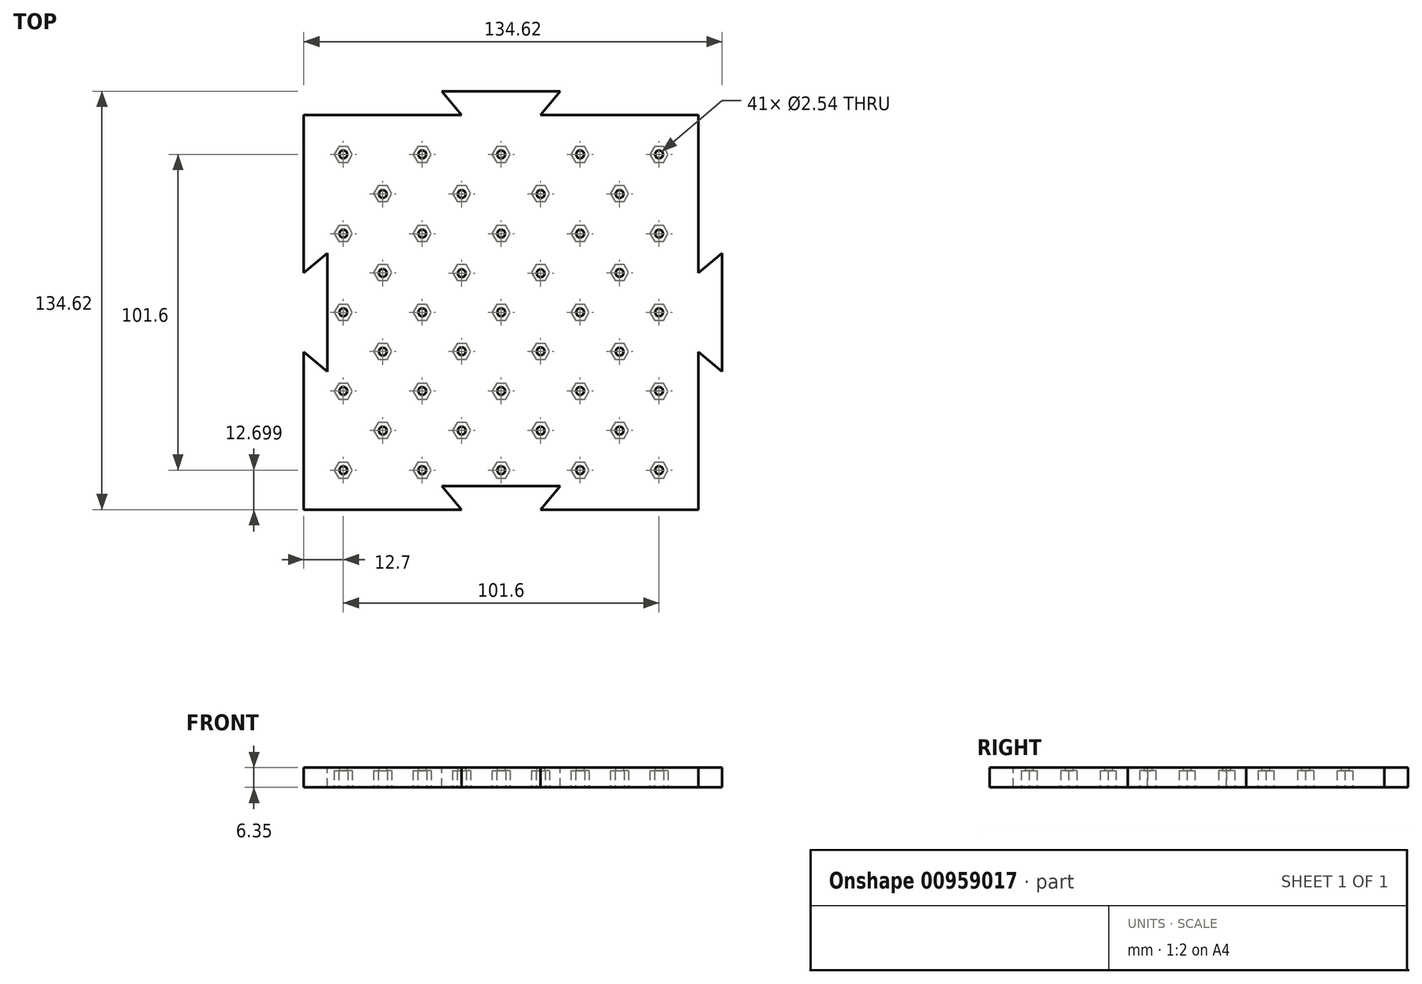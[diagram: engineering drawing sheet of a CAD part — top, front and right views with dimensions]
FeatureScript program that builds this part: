
annotation { "Feature Type Name" : "Feature", "Feature Type Description" : "" }
export const myFeature = defineFeature(function(context is Context, id is Id, definition is map)
    precondition{}
    {
        {
            var Q0;
            Q0=qCreatedBy(makeId("Top.planeOp"),FACE);
            var sketch = newSketch(context, id + "F0", { "sketchPlane" : qUnion([Q0])});
            skLineSegment(sketch, "E0.bottom", {"start": v(63.5, 63.69) * mm, "end": v(-63.5, 63.69) * mm});
            skLineSegment(sketch, "E0.top", {"start": v(63.5, -63.31) * mm, "end": v(-63.5, -63.31) * mm});
            skLineSegment(sketch, "E0.left", {"start": v(63.5, 63.69) * mm, "end": v(63.5, -63.31) * mm});
            skLineSegment(sketch, "E0.right", {"start": v(-63.5, 63.69) * mm, "end": v(-63.5, -63.31) * mm});
            skLineSegment(sketch, "E1", {"start": v(-50.8, 50.99) * mm, "end": v(50.8, 50.99) * mm, "construction": true});
            skLineSegment(sketch, "E2", {"start": v(-50.8, 50.99) * mm, "end": v(-50.8, -50.61) * mm, "construction": true});
            skLineSegment(sketch, "E3", {"start": v(-50.8, -50.61) * mm, "end": v(50.8, -50.61) * mm, "construction": true});
            skLineSegment(sketch, "E4", {"start": v(50.8, 50.99) * mm, "end": v(50.8, -50.61) * mm, "construction": true});
            skLineSegment(sketch, "E5", {"start": v(0, 50.99) * mm, "end": v(0, -50.61) * mm, "construction": true});
            skLineSegment(sketch, "E6", {"start": v(25.4, 50.99) * mm, "end": v(25.4, -50.61) * mm, "construction": true});
            skLineSegment(sketch, "E7", {"start": v(-50.8, 0.19) * mm, "end": v(50.8, 0.19) * mm, "construction": true});
            skLineSegment(sketch, "E8", {"start": v(-50.8, 0.19) * mm, "end": v(-25.4, 25.5) * mm, "construction": true});
            skLineSegment(sketch, "E9", {"start": v(-25.4, 25.5) * mm, "end": v(0, 50.99) * mm, "construction": true});
            skLineSegment(sketch, "E10", {"start": v(0, 0) * mm, "end": v(-25.4, 25.5) * mm, "construction": true});
            skLineSegment(sketch, "E11", {"start": v(-50.8, 50.99) * mm, "end": v(-25.4, 25.5) * mm, "construction": true});
            skLineSegment(sketch, "E12", {"start": v(-25.4, 50.99) * mm, "end": v(-25.4, -50.61) * mm, "construction": true});
            skCircle(sketch, "E13", {"center": v(-38.1, 38.24) * mm, "radius": 1.27 * mm});
            skCircle(sketch, "E14", {"center": v(-12.7, 38.24) * mm, "radius": 1.27 * mm});
            skCircle(sketch, "E15", {"center": v(-25.4, 25.5) * mm, "radius": 1.27 * mm});
            skCircle(sketch, "E16", {"center": v(-12.7, 12.75) * mm, "radius": 1.27 * mm});
            skCircle(sketch, "E17", {"center": v(-38.1, 12.84) * mm, "radius": 1.27 * mm});
            skCircle(sketch, "E18", {"center": v(0, 25.5) * mm, "radius": 1.27 * mm});
            skCircle(sketch, "E19", {"center": v(-25.4, 0.19) * mm, "radius": 1.27 * mm});
            skCircle(sketch, "E20.MirrorC", {"center": v(12.7, 38.24) * mm, "radius": 1.27 * mm});
            skCircle(sketch, "E21.MirrorC", {"center": v(25.4, 25.5) * mm, "radius": 1.27 * mm});
            skCircle(sketch, "E22.MirrorC", {"center": v(38.1, 38.24) * mm, "radius": 1.27 * mm});
            skLineSegment(sketch, "E23.MirrorCS", {"start": v(25.4, 25.5) * mm, "end": v(0, 50.99) * mm, "construction": true});
            skLineSegment(sketch, "E24.MirrorCS", {"start": v(50.8, 50.99) * mm, "end": v(25.4, 25.5) * mm, "construction": true});
            skLineSegment(sketch, "E25.MirrorCS", {"start": v(0, 0) * mm, "end": v(25.4, 25.5) * mm, "construction": true});
            skLineSegment(sketch, "E26.MirrorCS", {"start": v(50.8, 0.19) * mm, "end": v(25.4, 25.5) * mm, "construction": true});
            skCircle(sketch, "E27.MirrorC", {"center": v(38.1, 12.84) * mm, "radius": 1.27 * mm});
            skCircle(sketch, "E28.MirrorC", {"center": v(12.7, 12.75) * mm, "radius": 1.27 * mm});
            skCircle(sketch, "E29.MirrorC", {"center": v(-25.4, -25.12) * mm, "radius": 1.27 * mm});
            skCircle(sketch, "E30.MirrorC", {"center": v(25.4, -25.12) * mm, "radius": 1.27 * mm});
            skCircle(sketch, "E31.MirrorC", {"center": v(12.7, -37.86) * mm, "radius": 1.27 * mm});
            skCircle(sketch, "E32.MirrorC", {"center": v(-38.1, -12.46) * mm, "radius": 1.27 * mm});
            skLineSegment(sketch, "E33.MirrorCS", {"start": v(25.4, -50.61) * mm, "end": v(25.4, 50.99) * mm, "construction": true});
            skCircle(sketch, "E34.MirrorC", {"center": v(-38.1, -37.86) * mm, "radius": 1.27 * mm});
            skCircle(sketch, "E35.MirrorC", {"center": v(38.1, -12.46) * mm, "radius": 1.27 * mm});
            skCircle(sketch, "E36.MirrorC", {"center": v(0, -25.12) * mm, "radius": 1.27 * mm});
            skCircle(sketch, "E37.MirrorC", {"center": v(-12.7, -37.86) * mm, "radius": 1.27 * mm});
            skCircle(sketch, "E38.MirrorC", {"center": v(38.1, -37.86) * mm, "radius": 1.27 * mm});
            skCircle(sketch, "E39.MirrorC", {"center": v(-12.7, -12.37) * mm, "radius": 1.27 * mm});
            skCircle(sketch, "E40.MirrorC", {"center": v(12.7, -12.37) * mm, "radius": 1.27 * mm});
            skLineSegment(sketch, "E41.MirrorCS", {"start": v(-25.4, -25.12) * mm, "end": v(0, -50.61) * mm, "construction": true});
            skLineSegment(sketch, "E42.MirrorCS", {"start": v(50.8, -50.61) * mm, "end": v(25.4, -25.12) * mm, "construction": true});
            skLineSegment(sketch, "E43.MirrorCS", {"start": v(-50.8, -50.61) * mm, "end": v(-25.4, -25.12) * mm, "construction": true});
            skLineSegment(sketch, "E44.MirrorCS", {"start": v(50.8, 0.19) * mm, "end": v(25.4, -25.12) * mm, "construction": true});
            skLineSegment(sketch, "E45.MirrorCS", {"start": v(0, 0.38) * mm, "end": v(25.4, -25.12) * mm, "construction": true});
            skLineSegment(sketch, "E46.MirrorCS", {"start": v(0, -50.61) * mm, "end": v(0, 50.99) * mm, "construction": true});
            skLineSegment(sketch, "E47.MirrorCS", {"start": v(-25.4, -50.61) * mm, "end": v(-25.4, 50.99) * mm, "construction": true});
            skLineSegment(sketch, "E48.MirrorCS", {"start": v(0, 0.38) * mm, "end": v(-25.4, -25.12) * mm, "construction": true});
            skLineSegment(sketch, "E49.MirrorCS", {"start": v(25.4, -25.12) * mm, "end": v(0, -50.61) * mm, "construction": true});
            skLineSegment(sketch, "E50.MirrorCS", {"start": v(-50.8, 0.19) * mm, "end": v(-25.4, -25.12) * mm, "construction": true});
            skCircle(sketch, "E51.MirrorC", {"center": v(25.4, 0.19) * mm, "radius": 1.27 * mm});
            skCircle(sketch, "E52", {"center": v(-50.8, 0.19) * mm, "radius": 1.27 * mm});
            skCircle(sketch, "E53", {"center": v(-50.8, -25.12) * mm, "radius": 1.27 * mm});
            skCircle(sketch, "E54", {"center": v(-50.8, 25.5) * mm, "radius": 1.27 * mm});
            skCircle(sketch, "E55", {"center": v(-50.8, 50.99) * mm, "radius": 1.27 * mm});
            skCircle(sketch, "E56", {"center": v(-50.8, -50.61) * mm, "radius": 1.27 * mm});
            skCircle(sketch, "E57", {"center": v(-25.4, -50.61) * mm, "radius": 1.27 * mm});
            skCircle(sketch, "E58", {"center": v(0, -50.61) * mm, "radius": 1.27 * mm});
            skCircle(sketch, "E59", {"center": v(25.4, -50.61) * mm, "radius": 1.27 * mm});
            skCircle(sketch, "E60", {"center": v(50.8, -50.61) * mm, "radius": 1.27 * mm});
            skCircle(sketch, "E61", {"center": v(50.8, -25.12) * mm, "radius": 1.27 * mm});
            skCircle(sketch, "E62", {"center": v(50.8, 0.19) * mm, "radius": 1.27 * mm});
            skCircle(sketch, "E63", {"center": v(50.8, 25.5) * mm, "radius": 1.27 * mm});
            skCircle(sketch, "E64", {"center": v(50.8, 50.99) * mm, "radius": 1.27 * mm});
            skCircle(sketch, "E65", {"center": v(25.4, 50.99) * mm, "radius": 1.27 * mm});
            skCircle(sketch, "E66", {"center": v(0, 50.99) * mm, "radius": 1.27 * mm});
            skCircle(sketch, "E67", {"center": v(-25.4, 50.99) * mm, "radius": 1.27 * mm});
            skCircle(sketch, "E68", {"center": v(0, 0.19) * mm, "radius": 1.27 * mm});
            skSolve(sketch);
        }
        {
            var Q0;
            Q0=makeQuery(id+"F0.imprint","IMPRINT",FACE,{"disambiguationData":[TD([[makeQuery(id+"F0.imprint","IMPRINT",EDGE,{"derivedFrom":sQuery(id+"F0.wireOp",EDGE,"E0.bottom")}),1.0]])]});
            extrude(context, id + "F1", {"entities" : qUnion([Q0]), "depth" : 6.35 * mm, "offsetDistance" : 25.4 * mm});
        }
        {
            var Q0;
            Q0=makeQuery(id+"F1.opExtrude","CAP_FACE",FACE,{"disambiguationData":[OSD([sQuery(id+"F0.wireOp",EDGE,"E0.bottom"),sQuery(id+"F0.wireOp",EDGE,"E0.top"),sQuery(id+"F0.wireOp",EDGE,"E0.left"),sQuery(id+"F0.wireOp",EDGE,"E0.right"),sQuery(id+"F0.wireOp",EDGE,"Hy7Gs1fu-bPC3-lwsH-q5tp-A8iLxPEHDNgU"),sQuery(id+"F0.wireOp",EDGE,"OdMErub8-gENd-RMHu-1Eyq-STtZkmv1sPD6"),sQuery(id+"F0.wireOp",EDGE,"gUio85Hi-duiy-LhhE-UZof-TjOPB2Q9psdY"),sQuery(id+"F0.wireOp",EDGE,"tl9tluQc-fSzx-BFO9-yEud-i3mXb7KbXmNx"),sQuery(id+"F0.wireOp",EDGE,"GmsfjQEB-c2r3-9ydc-1yJa-UPbpGBDKNwxx"),sQuery(id+"F0.wireOp",EDGE,"eb66b9ba-c206-47c9-b1f8-58a300546e6e.0.1.0"),sQuery(id+"F0.wireOp",EDGE,"eb66b9ba-c206-47c9-b1f8-58a300546e6e.0.1.1"),sQuery(id+"F0.wireOp",EDGE,"eb66b9ba-c206-47c9-b1f8-58a300546e6e.0.1.2"),sQuery(id+"F0.wireOp",EDGE,"eb66b9ba-c206-47c9-b1f8-58a300546e6e.0.1.3"),sQuery(id+"F0.wireOp",EDGE,"eb66b9ba-c206-47c9-b1f8-58a300546e6e.0.1.4"),sQuery(id+"F0.wireOp",EDGE,"eb66b9ba-c206-47c9-b1f8-58a300546e6e.1.0.0"),sQuery(id+"F0.wireOp",EDGE,"eb66b9ba-c206-47c9-b1f8-58a300546e6e.1.0.1"),sQuery(id+"F0.wireOp",EDGE,"eb66b9ba-c206-47c9-b1f8-58a300546e6e.1.0.2"),sQuery(id+"F0.wireOp",EDGE,"eb66b9ba-c206-47c9-b1f8-58a300546e6e.1.0.3"),sQuery(id+"F0.wireOp",EDGE,"eb66b9ba-c206-47c9-b1f8-58a300546e6e.1.0.4"),sQuery(id+"F0.wireOp",EDGE,"eb66b9ba-c206-47c9-b1f8-58a300546e6e.1.1.0"),sQuery(id+"F0.wireOp",EDGE,"eb66b9ba-c206-47c9-b1f8-58a300546e6e.1.1.1"),sQuery(id+"F0.wireOp",EDGE,"eb66b9ba-c206-47c9-b1f8-58a300546e6e.1.1.2"),sQuery(id+"F0.wireOp",EDGE,"eb66b9ba-c206-47c9-b1f8-58a300546e6e.1.1.3"),sQuery(id+"F0.wireOp",EDGE,"eb66b9ba-c206-47c9-b1f8-58a300546e6e.1.1.4")])],"isStart":true});
            var sketch = newSketch(context, id + "F2", { "sketchPlane" : qUnion([Q0])});
            skCircle(sketch, "E69.cCircle", {"center": v(-50.8, 50.61) * mm, "radius": 2.54 * mm, "construction": true});
            skLineSegment(sketch, "E69.0", {"start": v(-52.27, 53.15) * mm, "end": v(-49.33, 53.15) * mm});
            skLineSegment(sketch, "E69.1", {"start": v(-49.33, 53.15) * mm, "end": v(-47.87, 50.61) * mm});
            skLineSegment(sketch, "E69.2", {"start": v(-47.87, 50.61) * mm, "end": v(-49.33, 48.07) * mm});
            skLineSegment(sketch, "E69.3", {"start": v(-49.33, 48.07) * mm, "end": v(-52.27, 48.07) * mm});
            skLineSegment(sketch, "E69.4", {"start": v(-52.27, 48.07) * mm, "end": v(-53.73, 50.61) * mm});
            skLineSegment(sketch, "E69.5", {"start": v(-53.73, 50.61) * mm, "end": v(-52.27, 53.15) * mm});
            skPoint(sketch, "E69.0.midPoint", {"position": v(-50.8, 53.15) * mm});
            skCircle(sketch, "E70.cCircle", {"center": v(-38.1, 37.86) * mm, "radius": 2.54 * mm, "construction": true});
            skLineSegment(sketch, "E70.0", {"start": v(-39.57, 40.4) * mm, "end": v(-36.63, 40.4) * mm});
            skLineSegment(sketch, "E70.1", {"start": v(-36.63, 40.4) * mm, "end": v(-35.17, 37.86) * mm});
            skLineSegment(sketch, "E70.2", {"start": v(-35.17, 37.86) * mm, "end": v(-36.63, 35.32) * mm});
            skLineSegment(sketch, "E70.3", {"start": v(-36.63, 35.32) * mm, "end": v(-39.57, 35.32) * mm});
            skLineSegment(sketch, "E70.4", {"start": v(-39.57, 35.32) * mm, "end": v(-41.03, 37.86) * mm});
            skLineSegment(sketch, "E70.5", {"start": v(-41.03, 37.86) * mm, "end": v(-39.57, 40.4) * mm});
            skPoint(sketch, "E70.0.midPoint", {"position": v(-38.1, 40.4) * mm});
            skCircle(sketch, "E71.0.1.0", {"center": v(-38.1, 12.46) * mm, "radius": 2.54 * mm, "construction": true});
            skLineSegment(sketch, "E71.0.1.1", {"start": v(-36.63, 15) * mm, "end": v(-35.17, 12.46) * mm});
            skPoint(sketch, "E71.0.1.2", {"position": v(-38.1, 15) * mm});
            skLineSegment(sketch, "E71.0.1.3", {"start": v(-47.87, 25.21) * mm, "end": v(-49.33, 22.67) * mm});
            skLineSegment(sketch, "E71.0.1.4", {"start": v(-35.17, 12.46) * mm, "end": v(-36.63, 9.92) * mm});
            skLineSegment(sketch, "E71.0.1.5", {"start": v(-49.33, 27.75) * mm, "end": v(-47.87, 25.21) * mm});
            skPoint(sketch, "E71.0.1.6", {"position": v(-50.8, 27.75) * mm});
            skCircle(sketch, "E71.0.1.7", {"center": v(-50.8, 25.21) * mm, "radius": 2.54 * mm, "construction": true});
            skLineSegment(sketch, "E71.0.1.8", {"start": v(-52.27, 22.67) * mm, "end": v(-53.73, 25.21) * mm});
            skLineSegment(sketch, "E71.0.1.9", {"start": v(-41.03, 12.46) * mm, "end": v(-39.57, 15) * mm});
            skLineSegment(sketch, "E71.0.1.10", {"start": v(-49.33, 22.67) * mm, "end": v(-52.27, 22.67) * mm});
            skLineSegment(sketch, "E71.0.1.11", {"start": v(-53.73, 25.21) * mm, "end": v(-52.27, 27.75) * mm});
            skLineSegment(sketch, "E71.0.1.12", {"start": v(-52.27, 27.75) * mm, "end": v(-49.33, 27.75) * mm});
            skLineSegment(sketch, "E71.0.1.13", {"start": v(-39.57, 15) * mm, "end": v(-36.63, 15) * mm});
            skLineSegment(sketch, "E71.0.1.14", {"start": v(-39.57, 9.92) * mm, "end": v(-41.03, 12.46) * mm});
            skCircle(sketch, "E71.0.2.0", {"center": v(-38.1, -12.94) * mm, "radius": 2.54 * mm, "construction": true});
            skLineSegment(sketch, "E71.0.2.1", {"start": v(-36.63, -10.4) * mm, "end": v(-35.17, -12.94) * mm});
            skPoint(sketch, "E71.0.2.2", {"position": v(-38.1, -10.4) * mm});
            skLineSegment(sketch, "E71.0.2.3", {"start": v(-47.87, -0.19) * mm, "end": v(-49.33, -2.73) * mm});
            skLineSegment(sketch, "E71.0.2.4", {"start": v(-35.17, -12.94) * mm, "end": v(-36.63, -15.48) * mm});
            skLineSegment(sketch, "E71.0.2.5", {"start": v(-49.33, 2.35) * mm, "end": v(-47.87, -0.19) * mm});
            skPoint(sketch, "E71.0.2.6", {"position": v(-50.8, 2.35) * mm});
            skCircle(sketch, "E71.0.2.7", {"center": v(-50.8, -0.19) * mm, "radius": 2.54 * mm, "construction": true});
            skLineSegment(sketch, "E71.0.2.8", {"start": v(-52.27, -2.73) * mm, "end": v(-53.73, -0.19) * mm});
            skLineSegment(sketch, "E71.0.2.9", {"start": v(-41.03, -12.94) * mm, "end": v(-39.57, -10.4) * mm});
            skLineSegment(sketch, "E71.0.2.10", {"start": v(-49.33, -2.73) * mm, "end": v(-52.27, -2.73) * mm});
            skLineSegment(sketch, "E71.0.2.11", {"start": v(-53.73, -0.19) * mm, "end": v(-52.27, 2.35) * mm});
            skLineSegment(sketch, "E71.0.2.12", {"start": v(-52.27, 2.35) * mm, "end": v(-49.33, 2.35) * mm});
            skLineSegment(sketch, "E71.0.2.13", {"start": v(-39.57, -10.4) * mm, "end": v(-36.63, -10.4) * mm});
            skLineSegment(sketch, "E71.0.2.14", {"start": v(-39.57, -15.48) * mm, "end": v(-41.03, -12.94) * mm});
            skCircle(sketch, "E71.0.3.0", {"center": v(-38.1, -38.34) * mm, "radius": 2.54 * mm, "construction": true});
            skLineSegment(sketch, "E71.0.3.1", {"start": v(-36.63, -35.8) * mm, "end": v(-35.17, -38.34) * mm});
            skPoint(sketch, "E71.0.3.2", {"position": v(-38.1, -35.8) * mm});
            skLineSegment(sketch, "E71.0.3.3", {"start": v(-47.87, -25.59) * mm, "end": v(-49.33, -28.13) * mm});
            skLineSegment(sketch, "E71.0.3.4", {"start": v(-35.17, -38.34) * mm, "end": v(-36.63, -40.88) * mm});
            skLineSegment(sketch, "E71.0.3.5", {"start": v(-49.33, -23.05) * mm, "end": v(-47.87, -25.59) * mm});
            skPoint(sketch, "E71.0.3.6", {"position": v(-50.8, -23.05) * mm});
            skCircle(sketch, "E71.0.3.7", {"center": v(-50.8, -25.59) * mm, "radius": 2.54 * mm, "construction": true});
            skLineSegment(sketch, "E71.0.3.8", {"start": v(-52.27, -28.13) * mm, "end": v(-53.73, -25.59) * mm});
            skLineSegment(sketch, "E71.0.3.9", {"start": v(-41.03, -38.34) * mm, "end": v(-39.57, -35.8) * mm});
            skLineSegment(sketch, "E71.0.3.10", {"start": v(-49.33, -28.13) * mm, "end": v(-52.27, -28.13) * mm});
            skLineSegment(sketch, "E71.0.3.11", {"start": v(-53.73, -25.59) * mm, "end": v(-52.27, -23.05) * mm});
            skLineSegment(sketch, "E71.0.3.12", {"start": v(-52.27, -23.05) * mm, "end": v(-49.33, -23.05) * mm});
            skLineSegment(sketch, "E71.0.3.13", {"start": v(-39.57, -35.8) * mm, "end": v(-36.63, -35.8) * mm});
            skLineSegment(sketch, "E71.0.3.14", {"start": v(-39.57, -40.88) * mm, "end": v(-41.03, -38.34) * mm});
            skLineSegment(sketch, "E71.0.4.3", {"start": v(-47.87, -50.99) * mm, "end": v(-49.33, -53.53) * mm});
            skLineSegment(sketch, "E71.0.4.5", {"start": v(-49.33, -48.45) * mm, "end": v(-47.87, -50.99) * mm});
            skPoint(sketch, "E71.0.4.6", {"position": v(-50.8, -48.45) * mm});
            skCircle(sketch, "E71.0.4.7", {"center": v(-50.8, -50.99) * mm, "radius": 2.54 * mm, "construction": true});
            skLineSegment(sketch, "E71.0.4.8", {"start": v(-52.27, -53.53) * mm, "end": v(-53.73, -50.99) * mm});
            skLineSegment(sketch, "E71.0.4.10", {"start": v(-49.33, -53.53) * mm, "end": v(-52.27, -53.53) * mm});
            skLineSegment(sketch, "E71.0.4.11", {"start": v(-53.73, -50.99) * mm, "end": v(-52.27, -48.45) * mm});
            skLineSegment(sketch, "E71.0.4.12", {"start": v(-52.27, -48.45) * mm, "end": v(-49.33, -48.45) * mm});
            skCircle(sketch, "E71.1.0.0", {"center": v(-12.7, 37.86) * mm, "radius": 2.54 * mm, "construction": true});
            skLineSegment(sketch, "E71.1.0.1", {"start": v(-11.23, 40.4) * mm, "end": v(-9.77, 37.86) * mm});
            skPoint(sketch, "E71.1.0.2", {"position": v(-12.7, 40.4) * mm});
            skLineSegment(sketch, "E71.1.0.3", {"start": v(-22.47, 50.61) * mm, "end": v(-23.93, 48.07) * mm});
            skLineSegment(sketch, "E71.1.0.4", {"start": v(-9.77, 37.86) * mm, "end": v(-11.23, 35.32) * mm});
            skLineSegment(sketch, "E71.1.0.5", {"start": v(-23.93, 53.15) * mm, "end": v(-22.47, 50.61) * mm});
            skPoint(sketch, "E71.1.0.6", {"position": v(-25.4, 53.15) * mm});
            skCircle(sketch, "E71.1.0.7", {"center": v(-25.4, 50.61) * mm, "radius": 2.54 * mm, "construction": true});
            skLineSegment(sketch, "E71.1.0.8", {"start": v(-26.87, 48.07) * mm, "end": v(-28.33, 50.61) * mm});
            skLineSegment(sketch, "E71.1.0.9", {"start": v(-15.63, 37.86) * mm, "end": v(-14.17, 40.4) * mm});
            skLineSegment(sketch, "E71.1.0.10", {"start": v(-23.93, 48.07) * mm, "end": v(-26.87, 48.07) * mm});
            skLineSegment(sketch, "E71.1.0.11", {"start": v(-28.33, 50.61) * mm, "end": v(-26.87, 53.15) * mm});
            skLineSegment(sketch, "E71.1.0.12", {"start": v(-26.87, 53.15) * mm, "end": v(-23.93, 53.15) * mm});
            skLineSegment(sketch, "E71.1.0.13", {"start": v(-14.17, 40.4) * mm, "end": v(-11.23, 40.4) * mm});
            skLineSegment(sketch, "E71.1.0.14", {"start": v(-14.17, 35.32) * mm, "end": v(-15.63, 37.86) * mm});
            skCircle(sketch, "E71.1.1.0", {"center": v(-12.7, 12.46) * mm, "radius": 2.54 * mm, "construction": true});
            skLineSegment(sketch, "E71.1.1.1", {"start": v(-11.23, 15) * mm, "end": v(-9.77, 12.46) * mm});
            skPoint(sketch, "E71.1.1.2", {"position": v(-12.7, 15) * mm});
            skLineSegment(sketch, "E71.1.1.3", {"start": v(-22.47, 25.21) * mm, "end": v(-23.93, 22.67) * mm});
            skLineSegment(sketch, "E71.1.1.4", {"start": v(-9.77, 12.46) * mm, "end": v(-11.23, 9.92) * mm});
            skLineSegment(sketch, "E71.1.1.5", {"start": v(-23.93, 27.75) * mm, "end": v(-22.47, 25.21) * mm});
            skPoint(sketch, "E71.1.1.6", {"position": v(-25.4, 27.75) * mm});
            skCircle(sketch, "E71.1.1.7", {"center": v(-25.4, 25.21) * mm, "radius": 2.54 * mm, "construction": true});
            skLineSegment(sketch, "E71.1.1.8", {"start": v(-26.87, 22.67) * mm, "end": v(-28.33, 25.21) * mm});
            skLineSegment(sketch, "E71.1.1.9", {"start": v(-15.63, 12.46) * mm, "end": v(-14.17, 15) * mm});
            skLineSegment(sketch, "E71.1.1.10", {"start": v(-23.93, 22.67) * mm, "end": v(-26.87, 22.67) * mm});
            skLineSegment(sketch, "E71.1.1.11", {"start": v(-28.33, 25.21) * mm, "end": v(-26.87, 27.75) * mm});
            skLineSegment(sketch, "E71.1.1.12", {"start": v(-26.87, 27.75) * mm, "end": v(-23.93, 27.75) * mm});
            skLineSegment(sketch, "E71.1.1.13", {"start": v(-14.17, 15) * mm, "end": v(-11.23, 15) * mm});
            skLineSegment(sketch, "E71.1.1.14", {"start": v(-14.17, 9.92) * mm, "end": v(-15.63, 12.46) * mm});
            skCircle(sketch, "E71.1.2.0", {"center": v(-12.7, -12.94) * mm, "radius": 2.54 * mm, "construction": true});
            skLineSegment(sketch, "E71.1.2.1", {"start": v(-11.23, -10.4) * mm, "end": v(-9.77, -12.94) * mm});
            skPoint(sketch, "E71.1.2.2", {"position": v(-12.7, -10.4) * mm});
            skLineSegment(sketch, "E71.1.2.3", {"start": v(-22.47, -0.19) * mm, "end": v(-23.93, -2.73) * mm});
            skLineSegment(sketch, "E71.1.2.4", {"start": v(-9.77, -12.94) * mm, "end": v(-11.23, -15.48) * mm});
            skLineSegment(sketch, "E71.1.2.5", {"start": v(-23.93, 2.35) * mm, "end": v(-22.47, -0.19) * mm});
            skPoint(sketch, "E71.1.2.6", {"position": v(-25.4, 2.35) * mm});
            skCircle(sketch, "E71.1.2.7", {"center": v(-25.4, -0.19) * mm, "radius": 2.54 * mm, "construction": true});
            skLineSegment(sketch, "E71.1.2.8", {"start": v(-26.87, -2.73) * mm, "end": v(-28.33, -0.19) * mm});
            skLineSegment(sketch, "E71.1.2.9", {"start": v(-15.63, -12.94) * mm, "end": v(-14.17, -10.4) * mm});
            skLineSegment(sketch, "E71.1.2.10", {"start": v(-23.93, -2.73) * mm, "end": v(-26.87, -2.73) * mm});
            skLineSegment(sketch, "E71.1.2.11", {"start": v(-28.33, -0.19) * mm, "end": v(-26.87, 2.35) * mm});
            skLineSegment(sketch, "E71.1.2.12", {"start": v(-26.87, 2.35) * mm, "end": v(-23.93, 2.35) * mm});
            skLineSegment(sketch, "E71.1.2.13", {"start": v(-14.17, -10.4) * mm, "end": v(-11.23, -10.4) * mm});
            skLineSegment(sketch, "E71.1.2.14", {"start": v(-14.17, -15.48) * mm, "end": v(-15.63, -12.94) * mm});
            skCircle(sketch, "E71.1.3.0", {"center": v(-12.7, -38.34) * mm, "radius": 2.54 * mm, "construction": true});
            skLineSegment(sketch, "E71.1.3.1", {"start": v(-11.23, -35.8) * mm, "end": v(-9.77, -38.34) * mm});
            skPoint(sketch, "E71.1.3.2", {"position": v(-12.7, -35.8) * mm});
            skLineSegment(sketch, "E71.1.3.3", {"start": v(-22.47, -25.59) * mm, "end": v(-23.93, -28.13) * mm});
            skLineSegment(sketch, "E71.1.3.4", {"start": v(-9.77, -38.34) * mm, "end": v(-11.23, -40.88) * mm});
            skLineSegment(sketch, "E71.1.3.5", {"start": v(-23.93, -23.05) * mm, "end": v(-22.47, -25.59) * mm});
            skPoint(sketch, "E71.1.3.6", {"position": v(-25.4, -23.05) * mm});
            skCircle(sketch, "E71.1.3.7", {"center": v(-25.4, -25.59) * mm, "radius": 2.54 * mm, "construction": true});
            skLineSegment(sketch, "E71.1.3.8", {"start": v(-26.87, -28.13) * mm, "end": v(-28.33, -25.59) * mm});
            skLineSegment(sketch, "E71.1.3.9", {"start": v(-15.63, -38.34) * mm, "end": v(-14.17, -35.8) * mm});
            skLineSegment(sketch, "E71.1.3.10", {"start": v(-23.93, -28.13) * mm, "end": v(-26.87, -28.13) * mm});
            skLineSegment(sketch, "E71.1.3.11", {"start": v(-28.33, -25.59) * mm, "end": v(-26.87, -23.05) * mm});
            skLineSegment(sketch, "E71.1.3.12", {"start": v(-26.87, -23.05) * mm, "end": v(-23.93, -23.05) * mm});
            skLineSegment(sketch, "E71.1.3.13", {"start": v(-14.17, -35.8) * mm, "end": v(-11.23, -35.8) * mm});
            skLineSegment(sketch, "E71.1.3.14", {"start": v(-14.17, -40.88) * mm, "end": v(-15.63, -38.34) * mm});
            skLineSegment(sketch, "E71.1.4.3", {"start": v(-22.47, -50.99) * mm, "end": v(-23.93, -53.53) * mm});
            skLineSegment(sketch, "E71.1.4.5", {"start": v(-23.93, -48.45) * mm, "end": v(-22.47, -50.99) * mm});
            skPoint(sketch, "E71.1.4.6", {"position": v(-25.4, -48.45) * mm});
            skCircle(sketch, "E71.1.4.7", {"center": v(-25.4, -50.99) * mm, "radius": 2.54 * mm, "construction": true});
            skLineSegment(sketch, "E71.1.4.8", {"start": v(-26.87, -53.53) * mm, "end": v(-28.33, -50.99) * mm});
            skLineSegment(sketch, "E71.1.4.10", {"start": v(-23.93, -53.53) * mm, "end": v(-26.87, -53.53) * mm});
            skLineSegment(sketch, "E71.1.4.11", {"start": v(-28.33, -50.99) * mm, "end": v(-26.87, -48.45) * mm});
            skLineSegment(sketch, "E71.1.4.12", {"start": v(-26.87, -48.45) * mm, "end": v(-23.93, -48.45) * mm});
            skCircle(sketch, "E71.2.0.0", {"center": v(12.7, 37.86) * mm, "radius": 2.54 * mm, "construction": true});
            skLineSegment(sketch, "E71.2.0.1", {"start": v(14.17, 40.4) * mm, "end": v(15.63, 37.86) * mm});
            skPoint(sketch, "E71.2.0.2", {"position": v(12.7, 40.4) * mm});
            skLineSegment(sketch, "E71.2.0.3", {"start": v(2.93, 50.61) * mm, "end": v(1.47, 48.07) * mm});
            skLineSegment(sketch, "E71.2.0.4", {"start": v(15.63, 37.86) * mm, "end": v(14.17, 35.32) * mm});
            skLineSegment(sketch, "E71.2.0.5", {"start": v(1.47, 53.15) * mm, "end": v(2.93, 50.61) * mm});
            skPoint(sketch, "E71.2.0.6", {"position": v(0, 53.15) * mm});
            skCircle(sketch, "E71.2.0.7", {"center": v(0, 50.61) * mm, "radius": 2.54 * mm, "construction": true});
            skLineSegment(sketch, "E71.2.0.8", {"start": v(-1.47, 48.07) * mm, "end": v(-2.93, 50.61) * mm});
            skLineSegment(sketch, "E71.2.0.9", {"start": v(9.77, 37.86) * mm, "end": v(11.23, 40.4) * mm});
            skLineSegment(sketch, "E71.2.0.10", {"start": v(1.47, 48.07) * mm, "end": v(-1.47, 48.07) * mm});
            skLineSegment(sketch, "E71.2.0.11", {"start": v(-2.93, 50.61) * mm, "end": v(-1.47, 53.15) * mm});
            skLineSegment(sketch, "E71.2.0.12", {"start": v(-1.47, 53.15) * mm, "end": v(1.47, 53.15) * mm});
            skLineSegment(sketch, "E71.2.0.13", {"start": v(11.23, 40.4) * mm, "end": v(14.17, 40.4) * mm});
            skLineSegment(sketch, "E71.2.0.14", {"start": v(11.23, 35.32) * mm, "end": v(9.77, 37.86) * mm});
            skCircle(sketch, "E71.2.1.0", {"center": v(12.7, 12.46) * mm, "radius": 2.54 * mm, "construction": true});
            skLineSegment(sketch, "E71.2.1.1", {"start": v(14.17, 15) * mm, "end": v(15.63, 12.46) * mm});
            skPoint(sketch, "E71.2.1.2", {"position": v(12.7, 15) * mm});
            skLineSegment(sketch, "E71.2.1.3", {"start": v(2.93, 25.21) * mm, "end": v(1.47, 22.67) * mm});
            skLineSegment(sketch, "E71.2.1.4", {"start": v(15.63, 12.46) * mm, "end": v(14.17, 9.92) * mm});
            skLineSegment(sketch, "E71.2.1.5", {"start": v(1.47, 27.75) * mm, "end": v(2.93, 25.21) * mm});
            skPoint(sketch, "E71.2.1.6", {"position": v(0, 27.75) * mm});
            skCircle(sketch, "E71.2.1.7", {"center": v(0, 25.21) * mm, "radius": 2.54 * mm, "construction": true});
            skLineSegment(sketch, "E71.2.1.8", {"start": v(-1.47, 22.67) * mm, "end": v(-2.93, 25.21) * mm});
            skLineSegment(sketch, "E71.2.1.9", {"start": v(9.77, 12.46) * mm, "end": v(11.23, 15) * mm});
            skLineSegment(sketch, "E71.2.1.10", {"start": v(1.47, 22.67) * mm, "end": v(-1.47, 22.67) * mm});
            skLineSegment(sketch, "E71.2.1.11", {"start": v(-2.93, 25.21) * mm, "end": v(-1.47, 27.75) * mm});
            skLineSegment(sketch, "E71.2.1.12", {"start": v(-1.47, 27.75) * mm, "end": v(1.47, 27.75) * mm});
            skLineSegment(sketch, "E71.2.1.13", {"start": v(11.23, 15) * mm, "end": v(14.17, 15) * mm});
            skLineSegment(sketch, "E71.2.1.14", {"start": v(11.23, 9.92) * mm, "end": v(9.77, 12.46) * mm});
            skCircle(sketch, "E71.2.2.0", {"center": v(12.7, -12.94) * mm, "radius": 2.54 * mm, "construction": true});
            skLineSegment(sketch, "E71.2.2.1", {"start": v(14.17, -10.4) * mm, "end": v(15.63, -12.94) * mm});
            skPoint(sketch, "E71.2.2.2", {"position": v(12.7, -10.4) * mm});
            skLineSegment(sketch, "E71.2.2.3", {"start": v(2.93, -0.19) * mm, "end": v(1.47, -2.73) * mm});
            skLineSegment(sketch, "E71.2.2.4", {"start": v(15.63, -12.94) * mm, "end": v(14.17, -15.48) * mm});
            skLineSegment(sketch, "E71.2.2.5", {"start": v(1.47, 2.35) * mm, "end": v(2.93, -0.19) * mm});
            skPoint(sketch, "E71.2.2.6", {"position": v(0, 2.35) * mm});
            skCircle(sketch, "E71.2.2.7", {"center": v(0, -0.19) * mm, "radius": 2.54 * mm, "construction": true});
            skLineSegment(sketch, "E71.2.2.8", {"start": v(-1.47, -2.73) * mm, "end": v(-2.93, -0.19) * mm});
            skLineSegment(sketch, "E71.2.2.9", {"start": v(9.77, -12.94) * mm, "end": v(11.23, -10.4) * mm});
            skLineSegment(sketch, "E71.2.2.10", {"start": v(1.47, -2.73) * mm, "end": v(-1.47, -2.73) * mm});
            skLineSegment(sketch, "E71.2.2.11", {"start": v(-2.93, -0.19) * mm, "end": v(-1.47, 2.35) * mm});
            skLineSegment(sketch, "E71.2.2.12", {"start": v(-1.47, 2.35) * mm, "end": v(1.47, 2.35) * mm});
            skLineSegment(sketch, "E71.2.2.13", {"start": v(11.23, -10.4) * mm, "end": v(14.17, -10.4) * mm});
            skLineSegment(sketch, "E71.2.2.14", {"start": v(11.23, -15.48) * mm, "end": v(9.77, -12.94) * mm});
            skCircle(sketch, "E71.2.3.0", {"center": v(12.7, -38.34) * mm, "radius": 2.54 * mm, "construction": true});
            skLineSegment(sketch, "E71.2.3.1", {"start": v(14.17, -35.8) * mm, "end": v(15.63, -38.34) * mm});
            skPoint(sketch, "E71.2.3.2", {"position": v(12.7, -35.8) * mm});
            skLineSegment(sketch, "E71.2.3.3", {"start": v(2.93, -25.59) * mm, "end": v(1.47, -28.13) * mm});
            skLineSegment(sketch, "E71.2.3.4", {"start": v(15.63, -38.34) * mm, "end": v(14.17, -40.88) * mm});
            skLineSegment(sketch, "E71.2.3.5", {"start": v(1.47, -23.05) * mm, "end": v(2.93, -25.59) * mm});
            skPoint(sketch, "E71.2.3.6", {"position": v(0, -23.05) * mm});
            skCircle(sketch, "E71.2.3.7", {"center": v(0, -25.59) * mm, "radius": 2.54 * mm, "construction": true});
            skLineSegment(sketch, "E71.2.3.8", {"start": v(-1.47, -28.13) * mm, "end": v(-2.93, -25.59) * mm});
            skLineSegment(sketch, "E71.2.3.9", {"start": v(9.77, -38.34) * mm, "end": v(11.23, -35.8) * mm});
            skLineSegment(sketch, "E71.2.3.10", {"start": v(1.47, -28.13) * mm, "end": v(-1.47, -28.13) * mm});
            skLineSegment(sketch, "E71.2.3.11", {"start": v(-2.93, -25.59) * mm, "end": v(-1.47, -23.05) * mm});
            skLineSegment(sketch, "E71.2.3.12", {"start": v(-1.47, -23.05) * mm, "end": v(1.47, -23.05) * mm});
            skLineSegment(sketch, "E71.2.3.13", {"start": v(11.23, -35.8) * mm, "end": v(14.17, -35.8) * mm});
            skLineSegment(sketch, "E71.2.3.14", {"start": v(11.23, -40.88) * mm, "end": v(9.77, -38.34) * mm});
            skLineSegment(sketch, "E71.2.4.3", {"start": v(2.93, -50.99) * mm, "end": v(1.47, -53.53) * mm});
            skLineSegment(sketch, "E71.2.4.5", {"start": v(1.47, -48.45) * mm, "end": v(2.93, -50.99) * mm});
            skPoint(sketch, "E71.2.4.6", {"position": v(0, -48.45) * mm});
            skCircle(sketch, "E71.2.4.7", {"center": v(0, -50.99) * mm, "radius": 2.54 * mm, "construction": true});
            skLineSegment(sketch, "E71.2.4.8", {"start": v(-1.47, -53.53) * mm, "end": v(-2.93, -50.99) * mm});
            skLineSegment(sketch, "E71.2.4.10", {"start": v(1.47, -53.53) * mm, "end": v(-1.47, -53.53) * mm});
            skLineSegment(sketch, "E71.2.4.11", {"start": v(-2.93, -50.99) * mm, "end": v(-1.47, -48.45) * mm});
            skLineSegment(sketch, "E71.2.4.12", {"start": v(-1.47, -48.45) * mm, "end": v(1.47, -48.45) * mm});
            skCircle(sketch, "E71.3.0.0", {"center": v(38.1, 37.86) * mm, "radius": 2.54 * mm, "construction": true});
            skLineSegment(sketch, "E71.3.0.1", {"start": v(39.57, 40.4) * mm, "end": v(41.03, 37.86) * mm});
            skPoint(sketch, "E71.3.0.2", {"position": v(38.1, 40.4) * mm});
            skLineSegment(sketch, "E71.3.0.3", {"start": v(28.33, 50.61) * mm, "end": v(26.87, 48.07) * mm});
            skLineSegment(sketch, "E71.3.0.4", {"start": v(41.03, 37.86) * mm, "end": v(39.57, 35.32) * mm});
            skLineSegment(sketch, "E71.3.0.5", {"start": v(26.87, 53.15) * mm, "end": v(28.33, 50.61) * mm});
            skPoint(sketch, "E71.3.0.6", {"position": v(25.4, 53.15) * mm});
            skCircle(sketch, "E71.3.0.7", {"center": v(25.4, 50.61) * mm, "radius": 2.54 * mm, "construction": true});
            skLineSegment(sketch, "E71.3.0.8", {"start": v(23.93, 48.07) * mm, "end": v(22.47, 50.61) * mm});
            skLineSegment(sketch, "E71.3.0.9", {"start": v(35.17, 37.86) * mm, "end": v(36.63, 40.4) * mm});
            skLineSegment(sketch, "E71.3.0.10", {"start": v(26.87, 48.07) * mm, "end": v(23.93, 48.07) * mm});
            skLineSegment(sketch, "E71.3.0.11", {"start": v(22.47, 50.61) * mm, "end": v(23.93, 53.15) * mm});
            skLineSegment(sketch, "E71.3.0.12", {"start": v(23.93, 53.15) * mm, "end": v(26.87, 53.15) * mm});
            skLineSegment(sketch, "E71.3.0.13", {"start": v(36.63, 40.4) * mm, "end": v(39.57, 40.4) * mm});
            skLineSegment(sketch, "E71.3.0.14", {"start": v(36.63, 35.32) * mm, "end": v(35.17, 37.86) * mm});
            skCircle(sketch, "E71.3.1.0", {"center": v(38.1, 12.46) * mm, "radius": 2.54 * mm, "construction": true});
            skLineSegment(sketch, "E71.3.1.1", {"start": v(39.57, 15) * mm, "end": v(41.03, 12.46) * mm});
            skPoint(sketch, "E71.3.1.2", {"position": v(38.1, 15) * mm});
            skLineSegment(sketch, "E71.3.1.3", {"start": v(28.33, 25.21) * mm, "end": v(26.87, 22.67) * mm});
            skLineSegment(sketch, "E71.3.1.4", {"start": v(41.03, 12.46) * mm, "end": v(39.57, 9.92) * mm});
            skLineSegment(sketch, "E71.3.1.5", {"start": v(26.87, 27.75) * mm, "end": v(28.33, 25.21) * mm});
            skPoint(sketch, "E71.3.1.6", {"position": v(25.4, 27.75) * mm});
            skCircle(sketch, "E71.3.1.7", {"center": v(25.4, 25.21) * mm, "radius": 2.54 * mm, "construction": true});
            skLineSegment(sketch, "E71.3.1.8", {"start": v(23.93, 22.67) * mm, "end": v(22.47, 25.21) * mm});
            skLineSegment(sketch, "E71.3.1.9", {"start": v(35.17, 12.46) * mm, "end": v(36.63, 15) * mm});
            skLineSegment(sketch, "E71.3.1.10", {"start": v(26.87, 22.67) * mm, "end": v(23.93, 22.67) * mm});
            skLineSegment(sketch, "E71.3.1.11", {"start": v(22.47, 25.21) * mm, "end": v(23.93, 27.75) * mm});
            skLineSegment(sketch, "E71.3.1.12", {"start": v(23.93, 27.75) * mm, "end": v(26.87, 27.75) * mm});
            skLineSegment(sketch, "E71.3.1.13", {"start": v(36.63, 15) * mm, "end": v(39.57, 15) * mm});
            skLineSegment(sketch, "E71.3.1.14", {"start": v(36.63, 9.92) * mm, "end": v(35.17, 12.46) * mm});
            skCircle(sketch, "E71.3.2.0", {"center": v(38.1, -12.94) * mm, "radius": 2.54 * mm, "construction": true});
            skLineSegment(sketch, "E71.3.2.1", {"start": v(39.57, -10.4) * mm, "end": v(41.03, -12.94) * mm});
            skPoint(sketch, "E71.3.2.2", {"position": v(38.1, -10.4) * mm});
            skLineSegment(sketch, "E71.3.2.3", {"start": v(28.33, -0.19) * mm, "end": v(26.87, -2.73) * mm});
            skLineSegment(sketch, "E71.3.2.4", {"start": v(41.03, -12.94) * mm, "end": v(39.57, -15.48) * mm});
            skLineSegment(sketch, "E71.3.2.5", {"start": v(26.87, 2.35) * mm, "end": v(28.33, -0.19) * mm});
            skPoint(sketch, "E71.3.2.6", {"position": v(25.4, 2.35) * mm});
            skCircle(sketch, "E71.3.2.7", {"center": v(25.4, -0.19) * mm, "radius": 2.54 * mm, "construction": true});
            skLineSegment(sketch, "E71.3.2.8", {"start": v(23.93, -2.73) * mm, "end": v(22.47, -0.19) * mm});
            skLineSegment(sketch, "E71.3.2.9", {"start": v(35.17, -12.94) * mm, "end": v(36.63, -10.4) * mm});
            skLineSegment(sketch, "E71.3.2.10", {"start": v(26.87, -2.73) * mm, "end": v(23.93, -2.73) * mm});
            skLineSegment(sketch, "E71.3.2.11", {"start": v(22.47, -0.19) * mm, "end": v(23.93, 2.35) * mm});
            skLineSegment(sketch, "E71.3.2.12", {"start": v(23.93, 2.35) * mm, "end": v(26.87, 2.35) * mm});
            skLineSegment(sketch, "E71.3.2.13", {"start": v(36.63, -10.4) * mm, "end": v(39.57, -10.4) * mm});
            skLineSegment(sketch, "E71.3.2.14", {"start": v(36.63, -15.48) * mm, "end": v(35.17, -12.94) * mm});
            skCircle(sketch, "E71.3.3.0", {"center": v(38.1, -38.34) * mm, "radius": 2.54 * mm, "construction": true});
            skLineSegment(sketch, "E71.3.3.1", {"start": v(39.57, -35.8) * mm, "end": v(41.03, -38.34) * mm});
            skPoint(sketch, "E71.3.3.2", {"position": v(38.1, -35.8) * mm});
            skLineSegment(sketch, "E71.3.3.3", {"start": v(28.33, -25.59) * mm, "end": v(26.87, -28.13) * mm});
            skLineSegment(sketch, "E71.3.3.4", {"start": v(41.03, -38.34) * mm, "end": v(39.57, -40.88) * mm});
            skLineSegment(sketch, "E71.3.3.5", {"start": v(26.87, -23.05) * mm, "end": v(28.33, -25.59) * mm});
            skPoint(sketch, "E71.3.3.6", {"position": v(25.4, -23.05) * mm});
            skCircle(sketch, "E71.3.3.7", {"center": v(25.4, -25.59) * mm, "radius": 2.54 * mm, "construction": true});
            skLineSegment(sketch, "E71.3.3.8", {"start": v(23.93, -28.13) * mm, "end": v(22.47, -25.59) * mm});
            skLineSegment(sketch, "E71.3.3.9", {"start": v(35.17, -38.34) * mm, "end": v(36.63, -35.8) * mm});
            skLineSegment(sketch, "E71.3.3.10", {"start": v(26.87, -28.13) * mm, "end": v(23.93, -28.13) * mm});
            skLineSegment(sketch, "E71.3.3.11", {"start": v(22.47, -25.59) * mm, "end": v(23.93, -23.05) * mm});
            skLineSegment(sketch, "E71.3.3.12", {"start": v(23.93, -23.05) * mm, "end": v(26.87, -23.05) * mm});
            skLineSegment(sketch, "E71.3.3.13", {"start": v(36.63, -35.8) * mm, "end": v(39.57, -35.8) * mm});
            skLineSegment(sketch, "E71.3.3.14", {"start": v(36.63, -40.88) * mm, "end": v(35.17, -38.34) * mm});
            skLineSegment(sketch, "E71.3.4.3", {"start": v(28.33, -50.99) * mm, "end": v(26.87, -53.53) * mm});
            skLineSegment(sketch, "E71.3.4.5", {"start": v(26.87, -48.45) * mm, "end": v(28.33, -50.99) * mm});
            skPoint(sketch, "E71.3.4.6", {"position": v(25.4, -48.45) * mm});
            skCircle(sketch, "E71.3.4.7", {"center": v(25.4, -50.99) * mm, "radius": 2.54 * mm, "construction": true});
            skLineSegment(sketch, "E71.3.4.8", {"start": v(23.93, -53.53) * mm, "end": v(22.47, -50.99) * mm});
            skLineSegment(sketch, "E71.3.4.10", {"start": v(26.87, -53.53) * mm, "end": v(23.93, -53.53) * mm});
            skLineSegment(sketch, "E71.3.4.11", {"start": v(22.47, -50.99) * mm, "end": v(23.93, -48.45) * mm});
            skLineSegment(sketch, "E71.3.4.12", {"start": v(23.93, -48.45) * mm, "end": v(26.87, -48.45) * mm});
            skLineSegment(sketch, "E71.4.0.3", {"start": v(53.73, 50.61) * mm, "end": v(52.27, 48.07) * mm});
            skLineSegment(sketch, "E71.4.0.5", {"start": v(52.27, 53.15) * mm, "end": v(53.73, 50.61) * mm});
            skPoint(sketch, "E71.4.0.6", {"position": v(50.8, 53.15) * mm});
            skCircle(sketch, "E71.4.0.7", {"center": v(50.8, 50.61) * mm, "radius": 2.54 * mm, "construction": true});
            skLineSegment(sketch, "E71.4.0.8", {"start": v(49.33, 48.07) * mm, "end": v(47.87, 50.61) * mm});
            skLineSegment(sketch, "E71.4.0.10", {"start": v(52.27, 48.07) * mm, "end": v(49.33, 48.07) * mm});
            skLineSegment(sketch, "E71.4.0.11", {"start": v(47.87, 50.61) * mm, "end": v(49.33, 53.15) * mm});
            skLineSegment(sketch, "E71.4.0.12", {"start": v(49.33, 53.15) * mm, "end": v(52.27, 53.15) * mm});
            skLineSegment(sketch, "E71.4.1.3", {"start": v(53.73, 25.21) * mm, "end": v(52.27, 22.67) * mm});
            skLineSegment(sketch, "E71.4.1.5", {"start": v(52.27, 27.75) * mm, "end": v(53.73, 25.21) * mm});
            skPoint(sketch, "E71.4.1.6", {"position": v(50.8, 27.75) * mm});
            skCircle(sketch, "E71.4.1.7", {"center": v(50.8, 25.21) * mm, "radius": 2.54 * mm, "construction": true});
            skLineSegment(sketch, "E71.4.1.8", {"start": v(49.33, 22.67) * mm, "end": v(47.87, 25.21) * mm});
            skLineSegment(sketch, "E71.4.1.10", {"start": v(52.27, 22.67) * mm, "end": v(49.33, 22.67) * mm});
            skLineSegment(sketch, "E71.4.1.11", {"start": v(47.87, 25.21) * mm, "end": v(49.33, 27.75) * mm});
            skLineSegment(sketch, "E71.4.1.12", {"start": v(49.33, 27.75) * mm, "end": v(52.27, 27.75) * mm});
            skLineSegment(sketch, "E71.4.2.3", {"start": v(53.73, -0.19) * mm, "end": v(52.27, -2.73) * mm});
            skLineSegment(sketch, "E71.4.2.5", {"start": v(52.27, 2.35) * mm, "end": v(53.73, -0.19) * mm});
            skPoint(sketch, "E71.4.2.6", {"position": v(50.8, 2.35) * mm});
            skCircle(sketch, "E71.4.2.7", {"center": v(50.8, -0.19) * mm, "radius": 2.54 * mm, "construction": true});
            skLineSegment(sketch, "E71.4.2.8", {"start": v(49.33, -2.73) * mm, "end": v(47.87, -0.19) * mm});
            skLineSegment(sketch, "E71.4.2.10", {"start": v(52.27, -2.73) * mm, "end": v(49.33, -2.73) * mm});
            skLineSegment(sketch, "E71.4.2.11", {"start": v(47.87, -0.19) * mm, "end": v(49.33, 2.35) * mm});
            skLineSegment(sketch, "E71.4.2.12", {"start": v(49.33, 2.35) * mm, "end": v(52.27, 2.35) * mm});
            skLineSegment(sketch, "E71.4.3.3", {"start": v(53.73, -25.59) * mm, "end": v(52.27, -28.13) * mm});
            skLineSegment(sketch, "E71.4.3.5", {"start": v(52.27, -23.05) * mm, "end": v(53.73, -25.59) * mm});
            skPoint(sketch, "E71.4.3.6", {"position": v(50.8, -23.05) * mm});
            skCircle(sketch, "E71.4.3.7", {"center": v(50.8, -25.59) * mm, "radius": 2.54 * mm, "construction": true});
            skLineSegment(sketch, "E71.4.3.8", {"start": v(49.33, -28.13) * mm, "end": v(47.87, -25.59) * mm});
            skLineSegment(sketch, "E71.4.3.10", {"start": v(52.27, -28.13) * mm, "end": v(49.33, -28.13) * mm});
            skLineSegment(sketch, "E71.4.3.11", {"start": v(47.87, -25.59) * mm, "end": v(49.33, -23.05) * mm});
            skLineSegment(sketch, "E71.4.3.12", {"start": v(49.33, -23.05) * mm, "end": v(52.27, -23.05) * mm});
            skLineSegment(sketch, "E71.4.4.3", {"start": v(53.73, -50.99) * mm, "end": v(52.27, -53.53) * mm});
            skLineSegment(sketch, "E71.4.4.5", {"start": v(52.27, -48.45) * mm, "end": v(53.73, -50.99) * mm});
            skPoint(sketch, "E71.4.4.6", {"position": v(50.8, -48.45) * mm});
            skCircle(sketch, "E71.4.4.7", {"center": v(50.8, -50.99) * mm, "radius": 2.54 * mm, "construction": true});
            skLineSegment(sketch, "E71.4.4.8", {"start": v(49.33, -53.53) * mm, "end": v(47.87, -50.99) * mm});
            skLineSegment(sketch, "E71.4.4.10", {"start": v(52.27, -53.53) * mm, "end": v(49.33, -53.53) * mm});
            skLineSegment(sketch, "E71.4.4.11", {"start": v(47.87, -50.99) * mm, "end": v(49.33, -48.45) * mm});
            skLineSegment(sketch, "E71.4.4.12", {"start": v(49.33, -48.45) * mm, "end": v(52.27, -48.45) * mm});
            skLineSegment(sketch, "E71.direction2", {"start": v(-39.57, 35.32) * mm, "end": v(-39.57, 9.92) * mm, "construction": true});
            skLineSegment(sketch, "E72.0.1.0", {"start": v(-36.63, 9.92) * mm, "end": v(-39.57, 9.92) * mm});
            skLineSegment(sketch, "E72.0.2.0", {"start": v(-36.63, -15.48) * mm, "end": v(-39.57, -15.48) * mm});
            skLineSegment(sketch, "E72.0.3.0", {"start": v(-36.63, -40.88) * mm, "end": v(-39.57, -40.88) * mm});
            skLineSegment(sketch, "E72.1.0.0", {"start": v(-11.23, 35.32) * mm, "end": v(-14.17, 35.32) * mm});
            skLineSegment(sketch, "E72.1.1.0", {"start": v(-11.23, 9.92) * mm, "end": v(-14.17, 9.92) * mm});
            skLineSegment(sketch, "E72.1.2.0", {"start": v(-11.23, -15.48) * mm, "end": v(-14.17, -15.48) * mm});
            skLineSegment(sketch, "E72.1.3.0", {"start": v(-11.23, -40.88) * mm, "end": v(-14.17, -40.88) * mm});
            skLineSegment(sketch, "E72.2.0.0", {"start": v(14.17, 35.32) * mm, "end": v(11.23, 35.32) * mm});
            skLineSegment(sketch, "E72.2.1.0", {"start": v(14.17, 9.92) * mm, "end": v(11.23, 9.92) * mm});
            skLineSegment(sketch, "E72.2.2.0", {"start": v(14.17, -15.48) * mm, "end": v(11.23, -15.48) * mm});
            skLineSegment(sketch, "E72.2.3.0", {"start": v(14.17, -40.88) * mm, "end": v(11.23, -40.88) * mm});
            skLineSegment(sketch, "E72.3.0.0", {"start": v(39.57, 35.32) * mm, "end": v(36.63, 35.32) * mm});
            skLineSegment(sketch, "E72.3.1.0", {"start": v(39.57, 9.92) * mm, "end": v(36.63, 9.92) * mm});
            skLineSegment(sketch, "E72.3.2.0", {"start": v(39.57, -15.48) * mm, "end": v(36.63, -15.48) * mm});
            skLineSegment(sketch, "E72.3.3.0", {"start": v(39.57, -40.88) * mm, "end": v(36.63, -40.88) * mm});
            skLineSegment(sketch, "E72.direction1", {"start": v(-39.57, 35.32) * mm, "end": v(-14.17, 35.32) * mm, "construction": true});
            skSolve(sketch);
        }
        {
            var Q0;
            Q0 = qSketchRegion(id + "F2", true);
            extrude(context, id + "F3", {"entities" : qUnion([Q0]), "operationType" : NewBodyOperationType.REMOVE, "oppositeDirection" : true, "depth" : 5.33 * mm, "offsetDistance" : 25.4 * mm});
        }
        {
            var Q0;
            Q0=makeQuery(id+"F1.opExtrude","CAP_FACE",FACE,{"disambiguationData":[OSD([sQuery(id+"F0.wireOp",EDGE,"E0.bottom"),sQuery(id+"F0.wireOp",EDGE,"E0.top"),sQuery(id+"F0.wireOp",EDGE,"E0.left"),sQuery(id+"F0.wireOp",EDGE,"E0.right"),sQuery(id+"F0.wireOp",EDGE,"Hy7Gs1fu-bPC3-lwsH-q5tp-A8iLxPEHDNgU"),sQuery(id+"F0.wireOp",EDGE,"OdMErub8-gENd-RMHu-1Eyq-STtZkmv1sPD6"),sQuery(id+"F0.wireOp",EDGE,"gUio85Hi-duiy-LhhE-UZof-TjOPB2Q9psdY"),sQuery(id+"F0.wireOp",EDGE,"tl9tluQc-fSzx-BFO9-yEud-i3mXb7KbXmNx"),sQuery(id+"F0.wireOp",EDGE,"GmsfjQEB-c2r3-9ydc-1yJa-UPbpGBDKNwxx"),sQuery(id+"F0.wireOp",EDGE,"eb66b9ba-c206-47c9-b1f8-58a300546e6e.0.1.0"),sQuery(id+"F0.wireOp",EDGE,"eb66b9ba-c206-47c9-b1f8-58a300546e6e.0.1.1"),sQuery(id+"F0.wireOp",EDGE,"eb66b9ba-c206-47c9-b1f8-58a300546e6e.0.1.2"),sQuery(id+"F0.wireOp",EDGE,"eb66b9ba-c206-47c9-b1f8-58a300546e6e.0.1.3"),sQuery(id+"F0.wireOp",EDGE,"eb66b9ba-c206-47c9-b1f8-58a300546e6e.0.1.4"),sQuery(id+"F0.wireOp",EDGE,"eb66b9ba-c206-47c9-b1f8-58a300546e6e.1.0.0"),sQuery(id+"F0.wireOp",EDGE,"eb66b9ba-c206-47c9-b1f8-58a300546e6e.1.0.1"),sQuery(id+"F0.wireOp",EDGE,"eb66b9ba-c206-47c9-b1f8-58a300546e6e.1.0.2"),sQuery(id+"F0.wireOp",EDGE,"eb66b9ba-c206-47c9-b1f8-58a300546e6e.1.0.3"),sQuery(id+"F0.wireOp",EDGE,"eb66b9ba-c206-47c9-b1f8-58a300546e6e.1.0.4"),sQuery(id+"F0.wireOp",EDGE,"eb66b9ba-c206-47c9-b1f8-58a300546e6e.1.1.0"),sQuery(id+"F0.wireOp",EDGE,"eb66b9ba-c206-47c9-b1f8-58a300546e6e.1.1.1"),sQuery(id+"F0.wireOp",EDGE,"eb66b9ba-c206-47c9-b1f8-58a300546e6e.1.1.2"),sQuery(id+"F0.wireOp",EDGE,"eb66b9ba-c206-47c9-b1f8-58a300546e6e.1.1.3"),sQuery(id+"F0.wireOp",EDGE,"eb66b9ba-c206-47c9-b1f8-58a300546e6e.1.1.4")])],"isStart":false});
            var sketch = newSketch(context, id + "F4", { "sketchPlane" : qUnion([Q0])});
            skLineSegment(sketch, "E73", {"start": v(-63.5, -63.31) * mm, "end": v(-12.7, -63.31) * mm});
            skLineSegment(sketch, "E74", {"start": v(63.5, -63.31) * mm, "end": v(12.7, -63.31) * mm});
            skLineSegment(sketch, "E75", {"start": v(0, -63.31) * mm, "end": v(0, -55.7) * mm});
            skLineSegment(sketch, "E76", {"start": v(0, -55.7) * mm, "end": v(-19.05, -55.7) * mm});
            skLineSegment(sketch, "E77", {"start": v(0, -55.7) * mm, "end": v(19.05, -55.7) * mm});
            skLineSegment(sketch, "E78", {"start": v(12.7, -63.31) * mm, "end": v(19.05, -55.7) * mm});
            skLineSegment(sketch, "E79", {"start": v(-12.7, -63.31) * mm, "end": v(-19.05, -55.7) * mm});
            skLineSegment(sketch, "E80", {"start": v(-63.5, 0.19) * mm, "end": v(63.5, 0.19) * mm, "construction": true});
            skLineSegment(sketch, "E81", {"start": v(-19.05, 56.07) * mm, "end": v(-19.05, 71.3) * mm, "construction": true});
            skLineSegment(sketch, "E82", {"start": v(19.05, 56.07) * mm, "end": v(19.05, 71.3) * mm, "construction": true});
            skLineSegment(sketch, "E83", {"start": v(19.05, 71.3) * mm, "end": v(12.7, 63.69) * mm});
            skLineSegment(sketch, "E84", {"start": v(-12.7, 63.69) * mm, "end": v(-19.05, 71.3) * mm});
            skLineSegment(sketch, "E85", {"start": v(19.05, 71.3) * mm, "end": v(-19.05, 71.3) * mm});
            skLineSegment(sketch, "E86", {"start": v(-12.7, 63.69) * mm, "end": v(12.7, 63.69) * mm});
            skLineSegment(sketch, "E87", {"start": v(0, 63.69) * mm, "end": v(0, -63.31) * mm, "construction": true});
            skLineSegment(sketch, "E88", {"start": v(-63.5, 63.69) * mm, "end": v(-63.5, 12.89) * mm});
            skLineSegment(sketch, "E89", {"start": v(-63.5, -63.31) * mm, "end": v(-63.5, -12.51) * mm});
            skLineSegment(sketch, "E90", {"start": v(-63.5, 0.19) * mm, "end": v(-55.88, 0.19) * mm});
            skLineSegment(sketch, "E91", {"start": v(-55.88, 0.19) * mm, "end": v(-55.88, 19.24) * mm});
            skLineSegment(sketch, "E92", {"start": v(-55.88, 0.19) * mm, "end": v(-55.88, -18.86) * mm});
            skLineSegment(sketch, "E93", {"start": v(-63.5, 12.89) * mm, "end": v(-55.88, 19.24) * mm});
            skLineSegment(sketch, "E94", {"start": v(-63.5, -12.51) * mm, "end": v(-55.88, -18.86) * mm});
            skLineSegment(sketch, "E95", {"start": v(63.5, 0.19) * mm, "end": v(71.12, 0.19) * mm});
            skLineSegment(sketch, "E96", {"start": v(71.12, 0.19) * mm, "end": v(71.12, 19.24) * mm});
            skLineSegment(sketch, "E97", {"start": v(71.12, 0.19) * mm, "end": v(71.12, -18.86) * mm});
            skLineSegment(sketch, "E98", {"start": v(63.5, -12.51) * mm, "end": v(71.12, -18.86) * mm});
            skLineSegment(sketch, "E99", {"start": v(63.5, 12.89) * mm, "end": v(71.12, 19.24) * mm});
            skSolve(sketch);
        }
        {
            var Q0;
            Q0=makeQuery(id+"F4.imprint","IMPRINT",FACE,{"disambiguationData":[TD([[makeQuery(id+"F4.imprint","IMPRINT",EDGE,{"derivedFrom":sQuery(id+"F4.wireOp",EDGE,"E83")}),-1.0]])]});
            var Q1;
            {var subQ0=sQuery(id+"F4.wireOp",EDGE,"E95");Q1=makeQuery(id+"F4.imprint","IMPRINT",FACE,{"disambiguationData":[TD([[makeQuery(id+"F4.imprint","IMPRINT",EDGE,{"derivedFrom":subQ0}),1.0]])]});}
            var Q2;
            {var subQ0=sQuery(id+"F4.wireOp",EDGE,"E95");Q2=makeQuery(id+"F4.imprint","IMPRINT",FACE,{"disambiguationData":[TD([[makeQuery(id+"F4.imprint","IMPRINT",EDGE,{"derivedFrom":subQ0}),-1.0]])]});}
            extrude(context, id + "F5", {"entities" : qUnion([Q0, Q1, Q2]), "operationType" : NewBodyOperationType.ADD, "oppositeDirection" : true, "depth" : 6.35 * mm, "offsetDistance" : 25.4 * mm});
        }
        {
            var Q0;
            {var subQ0=sQuery(id+"F4.wireOp",EDGE,"E90");Q0=makeQuery(id+"F4.imprint","IMPRINT",FACE,{"disambiguationData":[TD([[makeQuery(id+"F4.imprint","IMPRINT",EDGE,{"derivedFrom":subQ0}),1.0]])]});}
            var Q1;
            {var subQ0=sQuery(id+"F4.wireOp",EDGE,"E90");Q1=makeQuery(id+"F4.imprint","IMPRINT",FACE,{"disambiguationData":[TD([[makeQuery(id+"F4.imprint","IMPRINT",EDGE,{"derivedFrom":subQ0}),-1.0]])]});}
            var Q2;
            {var subQ0=sQuery(id+"F4.wireOp",EDGE,"E75");Q2=makeQuery(id+"F4.imprint","IMPRINT",FACE,{"disambiguationData":[TD([[makeQuery(id+"F4.imprint","IMPRINT",EDGE,{"derivedFrom":subQ0}),1.0]])]});}
            var Q3;
            {var subQ0=sQuery(id+"F4.wireOp",EDGE,"E75");Q3=makeQuery(id+"F4.imprint","IMPRINT",FACE,{"disambiguationData":[TD([[makeQuery(id+"F4.imprint","IMPRINT",EDGE,{"derivedFrom":subQ0}),-1.0]])]});}
            extrude(context, id + "F6", {"entities" : qUnion([Q0, Q1, Q2, Q3]), "operationType" : NewBodyOperationType.REMOVE, "endBound" : BoundingType.THROUGH_ALL, "oppositeDirection" : true, "depth" : 25.4 * mm, "offsetDistance" : 25.4 * mm});
        }
    });
